# Revit family: dl_50_iq_mini___st0_8a_5xa248c31f08he_9510
name_source: partatom
category: Lighting Fixtures
units: mm (PartAtom-declared; Revit-internal decimal feet)

## family parameters
Cut with Voids When Loaded = No
Host = Face
Light Source = No
Part Type = Normal
Room Calculation Point = No
Round Connector Dimension = Use Diameter
Shared = No

## types (1)
- --- (1 x LED, 9400 lm, 68.6 W, 3000K)
    Apparent Load = 69 VA
    CIE Flux Codes = 38 75 97 100 100
    Color Rendering = 70
    Color Temperature = 3000K
    Default Elevation = 1800 mm
    Description = DL 50 iQ mini, mast luminaire, primary light control with lens, of PMMA, primary optical cover: cover, of toughened safety glass, transparent, light distribution: ST0.8a, light emission: direct distribution, primary light characteristic: asymmetric, installation type: side-entry, post-top, LED, High Power LED, rated luminous flux: 9.400lm, luminous efficacy: 137lm/W, light colour: 730, colour temperature: 3000K, control gear: iQ Street-Remote, control: optimised constant luminous flux control (CLO 2.0), Desk-Remote (wireless, voltage-free reading and setting of iQ features in the workshop via application-optimized NFC function/RFID function), Light-Fading, Smart-Wire, Night-Set, Lumen-Switch, Temp-Guard, Auto-Match, Street-Remote, mains connection: 230..240V, AC, 50/60Hz, connection cable pre-assembled, cable length: 8,5m, start of lifetime: 69W, end of service life: 72W, reduction: 30W, luminaire housing, of diecast aluminium, powder-coated, SITECO metallic grey (DB 702S), inclination adjustable: 0°, 5°, 10° (post-top) | 0°, -5°, -10°, -15° (side-entry), please order mast post-top element or mast side-entry element separately, diameter: 500mm, height: 115mm, post-top: for spigot size d x l = 76 x 100mm; with reducer (optional accessory) 60 x 100mm | side-entry: for spigot size d x l = 60 x 100mm; with reducer (optional accessory) 42 x 100mm, mounting height: 4..6m, protection rating (complete): IP66, insulation class (complete): insulation class II (safety insulation), certification: CE, ENEC, ENEC+, VDE, impact resistance: IK08, permissible operating ambient temperature for outdoor applications: -25..+40°C, standard-compliant lighting for roads and squares, packaging unit: 1 piece

Light Distribution: ST0.8a
    Height = 115 mm
    Lamp = 1 x LED
    Lamp Light Flux = 9400 lm
    Lamp Power = 68.6 W
    Lamp count = 1
    Length = 500 mm
    Luminous efficacy = 137 lm/W
    Manufacturer = Siteco
    ModVariant = No
    Model = 5XA248C31F08HE
    Number of Poles = 1
    OnlyDefault = Yes
    Power Factor = 1
    Product Name = DL 50 iQ mini | ST0.8a
    Product group = mast luminaire | pylon top
    ProductGroupID = 6100
    Protection Class = Protection class II
    Protection Degree = IP 66
    RLX_Detail_Level = 1
    RLX_Emergency_Light_Flux = 0 lm
    RLX_Emergency_Type = 0
    RLX_Emergency_Type_DB = No
    RlxData = <blob elided: 115721 chars, md5=4f44bbe7>
    Socket = socket
    Standby Power = 0 W
    System Light Flux = 9400 lm
    System Power = 69 W
    Type Comments = factory setting: luminous flux: 100 % | dim-lin: 254 | 693 mA
    Type Image = l_1251794.jpg
    URL = http://relux.com
    VarID = @adj_141085
    Voltage = 0 V
    Weight = 0.00 kg
    Width = 0 mm  [stored 0 ft]

note: [stored X ft] marks values corroborated as IEEE doubles in the binary element streams (Revit-internal decimal feet)

## geometry (parser evidence)
native form markers: Sweep x11
no freeform markers — native parametric forms only
